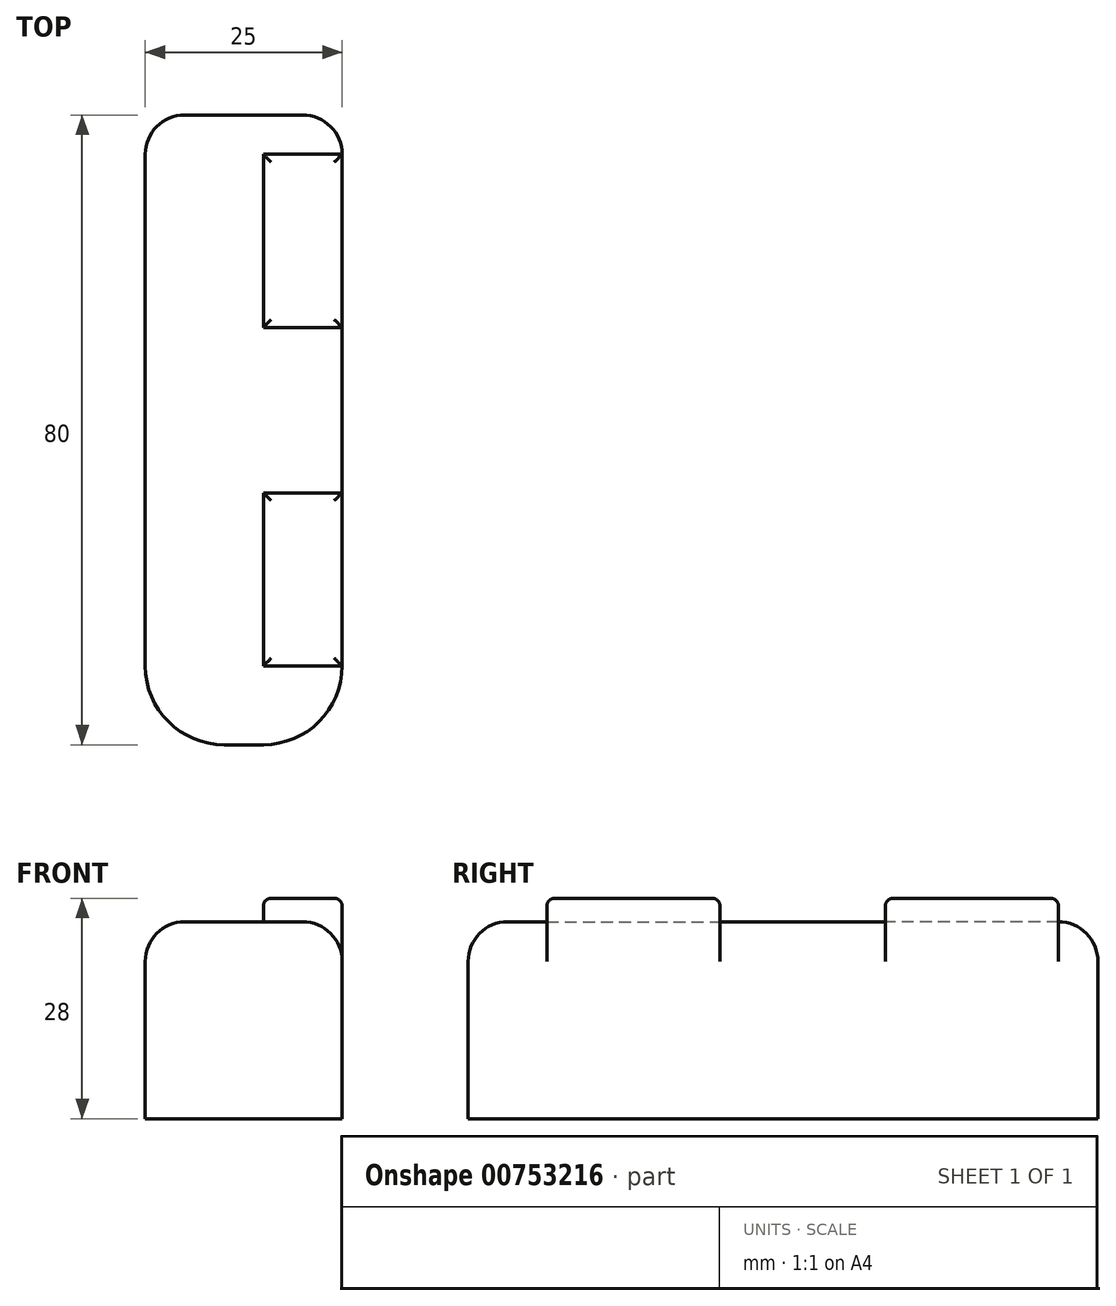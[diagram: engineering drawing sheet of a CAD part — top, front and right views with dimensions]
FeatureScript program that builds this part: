
annotation { "Feature Type Name" : "Feature", "Feature Type Description" : "" }
export const myFeature = defineFeature(function(context is Context, id is Id, definition is map)
    precondition{}
    {
        {
            var Q0;
            Q0=qCreatedBy(makeId("Top.planeOp"),FACE);
            var sketch = newSketch(context, id + "F0", { "sketchPlane" : qUnion([Q0])});
            skLineSegment(sketch, "E0.bottom", {"start": v(-33.98, -38.54) * mm, "end": v(52.97, -38.54) * mm});
            skLineSegment(sketch, "E0.top", {"start": v(-33.98, 53.37) * mm, "end": v(52.97, 53.37) * mm});
            skLineSegment(sketch, "E0.left", {"start": v(-33.98, -38.54) * mm, "end": v(-33.98, 53.37) * mm});
            skLineSegment(sketch, "E0.right", {"start": v(52.97, -38.54) * mm, "end": v(52.97, 53.37) * mm});
            skLineSegment(sketch, "E1.bottom", {"start": v(10, -20.96) * mm, "end": v(15, -20.96) * mm});
            skLineSegment(sketch, "E1.top", {"start": v(5, 59.04) * mm, "end": v(20, 59.04) * mm});
            skLineSegment(sketch, "E1.left", {"start": v(0, -10.96) * mm, "end": v(0, 54.04) * mm});
            skLineSegment(sketch, "E1.right", {"start": v(25, -10.96) * mm, "end": v(25, 54.04) * mm});
            skPoint(sketch, "E2.visualSharp", {"position": v(0, -20.96) * mm});
            skArc(sketch, "E2.filletArc", {"start": v(0, -10.96) * mm, "mid": v(2.93, -18.03) * mm, "end": v(10, -20.96) * mm});
            skPoint(sketch, "E3.visualSharp", {"position": v(25, -20.96) * mm});
            skArc(sketch, "E3.filletArc", {"start": v(15, -20.96) * mm, "mid": v(22.07, -18.03) * mm, "end": v(25, -10.96) * mm});
            skPoint(sketch, "E4.visualSharp", {"position": v(0, 59.04) * mm});
            skArc(sketch, "E4.filletArc", {"start": v(5, 59.04) * mm, "mid": v(1.46, 57.58) * mm, "end": v(0, 54.04) * mm});
            skPoint(sketch, "E5.visualSharp", {"position": v(25, 59.04) * mm});
            skArc(sketch, "E5.filletArc", {"start": v(25, 54.04) * mm, "mid": v(23.54, 57.58) * mm, "end": v(20, 59.04) * mm});
            skSolve(sketch);
        }
        {
            var Q0;
            Q0=makeQuery(id+"F0.imprint","IMPRINT",FACE,{"disambiguationData":[TD([[makeQuery(id+"F0.imprint","IMPRINT",EDGE,{"derivedFrom":sQuery(id+"F0.wireOp",EDGE,"E1.top")}),-1.0]])]});
            var Q1;
            Q1=makeQuery(id+"F0.imprint","IMPRINT",FACE,{"disambiguationData":[TD([[makeQuery(id+"F0.imprint","IMPRINT",EDGE,{"derivedFrom":sQuery(id+"F0.wireOp",EDGE,"E1.bottom")}),1.0]])]});
            extrude(context, id + "F1", {"entities" : qUnion([Q0, Q1]), "depth" : 25 * mm, "offsetDistance" : 25 * mm});
        }
        {
            var Q0;
            Q0=makeQuery(id+"F1.opExtrude","CAP_FACE",FACE,{"disambiguationData":[OSD([sQuery(id+"F0.wireOp",EDGE,"E1.bottom"),sQuery(id+"F0.wireOp",EDGE,"E1.top"),sQuery(id+"F0.wireOp",EDGE,"E1.left"),sQuery(id+"F0.wireOp",EDGE,"E1.right"),sQuery(id+"F0.wireOp",EDGE,"E2.filletArc"),sQuery(id+"F0.wireOp",EDGE,"E3.filletArc"),sQuery(id+"F0.wireOp",EDGE,"E4.filletArc"),sQuery(id+"F0.wireOp",EDGE,"E5.filletArc")])],"isStart":false});
            var sketch = newSketch(context, id + "F2", { "sketchPlane" : qUnion([Q0])});
            skLineSegment(sketch, "E6.bottom", {"start": v(25, -10.96) * mm, "end": v(15, -10.96) * mm});
            skLineSegment(sketch, "E6.top", {"start": v(25, 11.04) * mm, "end": v(15, 11.04) * mm});
            skLineSegment(sketch, "E6.left", {"start": v(25, -10.96) * mm, "end": v(25, 11.04) * mm});
            skLineSegment(sketch, "E6.right", {"start": v(15, -10.96) * mm, "end": v(15, 11.04) * mm});
            skLineSegment(sketch, "E7.bottom", {"start": v(25, 54.04) * mm, "end": v(15, 54.04) * mm});
            skLineSegment(sketch, "E7.top", {"start": v(25, 32.04) * mm, "end": v(15, 32.04) * mm});
            skLineSegment(sketch, "E7.left", {"start": v(25, 54.04) * mm, "end": v(25, 32.04) * mm});
            skLineSegment(sketch, "E7.right", {"start": v(15, 54.04) * mm, "end": v(15, 32.04) * mm});
            skSolve(sketch);
        }
        {
            var Q0;
            Q0 = qSketchRegion(id + "F2", true);
            extrude(context, id + "F3", {"entities" : qUnion([Q0]), "operationType" : NewBodyOperationType.ADD, "depth" : 3 * mm, "offsetDistance" : 25 * mm});
        }
        {
            var Q0;
            Q0=makeQuery(id+"F1.opExtrude","CAP_EDGE",EDGE,{"disambiguationData":[OSD([sQuery(id+"F0.wireOp",EDGE,"E1.right")])],"isStart":false});
            var Q1;
            Q1=makeQuery(id+"F1.opExtrude","CAP_EDGE",EDGE,{"disambiguationData":[OSD([sQuery(id+"F0.wireOp",EDGE,"E1.left")])],"isStart":false});
            fillet(context, id + "F4", {"entities" : qUnion([Q0, Q1]), "tangentPropagation" : true, "radius" : 5 * mm, "defaultsChanged" : false, "vertexSettings" : [], "allowEdgeOverflow" : false});
        }
        {
            var Q0;
            Q0=makeQuery(id+"F3.opExtrude","CAP_FACE",FACE,{"disambiguationData":[OSD([sQuery(id+"F2.wireOp",EDGE,"E6.bottom"),sQuery(id+"F2.wireOp",EDGE,"E6.top"),sQuery(id+"F2.wireOp",EDGE,"E6.left"),sQuery(id+"F2.wireOp",EDGE,"E6.right")])],"isStart":false});
            var Q1;
            Q1=makeQuery(id+"F3.opExtrude","CAP_FACE",FACE,{"disambiguationData":[OSD([sQuery(id+"F2.wireOp",EDGE,"E7.bottom"),sQuery(id+"F2.wireOp",EDGE,"E7.top"),sQuery(id+"F2.wireOp",EDGE,"E7.left"),sQuery(id+"F2.wireOp",EDGE,"E7.right")])],"isStart":false});
            fillet(context, id + "F5", {"entities" : qUnion([Q0, Q1]), "tangentPropagation" : true, "radius" : 1 * mm, "defaultsChanged" : false, "vertexSettings" : [], "allowEdgeOverflow" : false});
        }
    });
